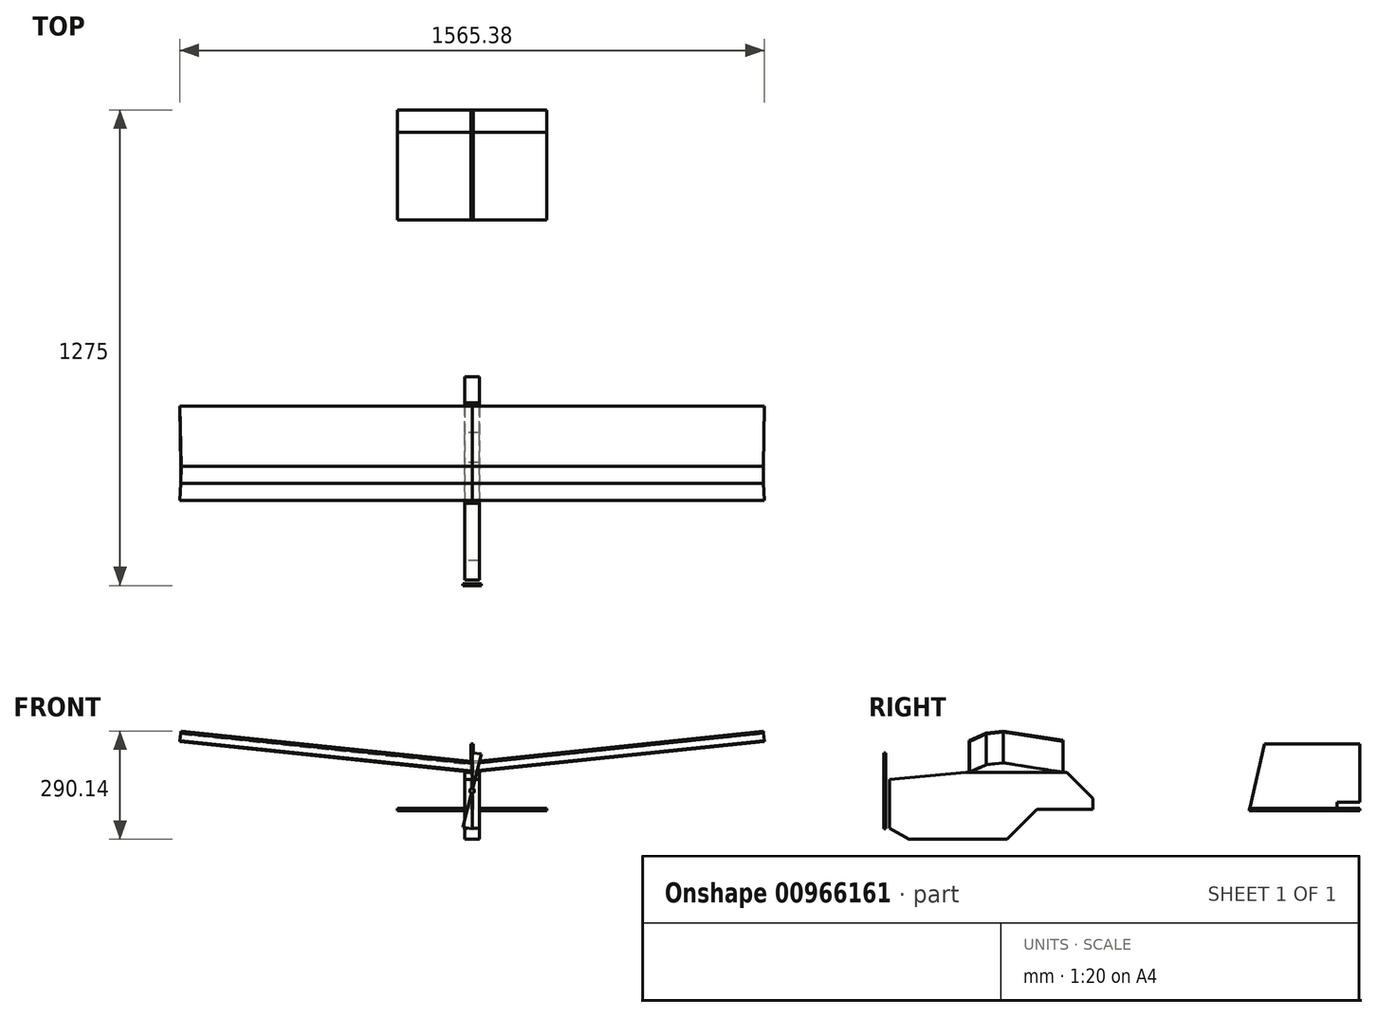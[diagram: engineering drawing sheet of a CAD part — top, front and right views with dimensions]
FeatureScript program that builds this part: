
annotation { "Feature Type Name" : "Feature", "Feature Type Description" : "" }
export const myFeature = defineFeature(function(context is Context, id is Id, definition is map)
    precondition{}
    {
        {
            var Q0;
            Q0=qCreatedBy(makeId("Right.planeOp"),FACE);
            var sketch = newSketch(context, id + "F0", { "sketchPlane" : qUnion([Q0])});
            skLineSegment(sketch, "E0", {"start": v(0, 0) * mm, "end": v(45, 20) * mm});
            skLineSegment(sketch, "E1", {"start": v(45, 20) * mm, "end": v(90, 25) * mm});
            skLineSegment(sketch, "E2", {"start": v(90, 25) * mm, "end": v(250, 0) * mm});
            skLineSegment(sketch, "E3.0", {"start": v(90.07, 28.03) * mm, "end": v(250.46, 2.96) * mm});
            skLineSegment(sketch, "E3.1", {"start": v(44.2, 22.93) * mm, "end": v(90.07, 28.03) * mm});
            skLineSegment(sketch, "E3.2", {"start": v(-1.22, 2.74) * mm, "end": v(44.2, 22.93) * mm});
            skLineSegment(sketch, "E4", {"start": v(0, 0) * mm, "end": v(-1.22, 2.74) * mm});
            skLineSegment(sketch, "E5", {"start": v(250, 0) * mm, "end": v(250.46, 2.96) * mm});
            skSolve(sketch);
        }
        {
            var Q0;
            Q0=makeQuery(id+"F0.imprint","IMPRINT",FACE,{"disambiguationData":[TD([[makeQuery(id+"F0.imprint","IMPRINT",EDGE,{"derivedFrom":sQuery(id+"F0.wireOp",EDGE,"E1")}),1.0]])]});
            var Q1;
            Q1=makeQuery(id+"F0.imprint","IMPRINT",FACE,{"disambiguationData":[TD([[makeQuery(id+"F0.imprint","IMPRINT",EDGE,{"derivedFrom":sQuery(id+"F0.wireOp",EDGE,"E0")}),1.0]])]});
            var Q2;
            Q2=makeQuery(id+"F0.imprint","IMPRINT",FACE,{"disambiguationData":[TD([[makeQuery(id+"F0.imprint","IMPRINT",EDGE,{"derivedFrom":sQuery(id+"F0.wireOp",EDGE,"E2")}),1.0]])]});
            extrude(context, id + "F1", {"entities" : qUnion([Q0, Q1, Q2]), "depth" : 787 * mm, "offsetDistance" : 25 * mm});
        }
        {
            var Q0;
            Q0=qCreatedBy(makeId("Front.planeOp"),FACE);
            var sketch = newSketch(context, id + "F2", { "sketchPlane" : qUnion([Q0])});
            skPoint(sketch, "E6.middle", {"position": v(0, 0) * mm});
            skLineSegment(sketch, "E7", {"start": v(0, 0) * mm, "end": v(32.96, -3.46) * mm, "construction": true});
            skLineSegment(sketch, "E8.bottom", {"start": v(0, 0) * mm, "end": v(-49.73, 5.23) * mm});
            skLineSegment(sketch, "E8.top", {"start": v(5.23, 49.73) * mm, "end": v(-44.5, 54.95) * mm});
            skLineSegment(sketch, "E8.left", {"start": v(0, 0) * mm, "end": v(5.23, 49.73) * mm});
            skLineSegment(sketch, "E8.right", {"start": v(-49.73, 5.23) * mm, "end": v(-44.5, 54.95) * mm});
            skSolve(sketch);
        }
        {
            var Q0;
            Q0=makeQuery(id+"F2.imprint","IMPRINT",FACE,{"disambiguationData":[TD([[makeQuery(id+"F2.imprint","IMPRINT",EDGE,{"derivedFrom":sQuery(id+"F2.wireOp",EDGE,"E8.bottom")}),-1.0]])]});
            extrude(context, id + "F3", {"entities" : qUnion([Q0]), "operationType" : NewBodyOperationType.REMOVE, "endBound" : BoundingType.THROUGH_ALL, "oppositeDirection" : true, "depth" : 300 * mm, "offsetDistance" : 25 * mm});
        }
        {
            var Q0;
            Q0=makeQuery(id+"F1.opExtrude","SWEPT_BODY",BODY,{"disambiguationData":[OSD([sQuery(id+"F0.wireOp",EDGE,"E0"),sQuery(id+"F0.wireOp",EDGE,"E1"),sQuery(id+"F0.wireOp",EDGE,"E2"),sQuery(id+"F0.wireOp",EDGE,"E3.0"),sQuery(id+"F0.wireOp",EDGE,"E3.1"),sQuery(id+"F0.wireOp",EDGE,"E3.2"),sQuery(id+"F0.wireOp",EDGE,"E4"),sQuery(id+"F0.wireOp",EDGE,"E5")])]});
            var Q1;
            Q1=qCreatedBy(makeId("Right.planeOp"),FACE);
            mirror(context, id + "F4", {"entities" : qUnion([Q0]), "mirrorPlane" : qUnion([Q1])});
        }
        {
            var Q0;
            Q0=qCreatedBy(makeId("Right.planeOp"),FACE);
            var sketch = newSketch(context, id + "F5", { "sketchPlane" : qUnion([Q0])});
            skLineSegment(sketch, "E9", {"start": v(-68.1, 0) * mm, "end": v(194.4, 0) * mm, "construction": true});
            skSolve(sketch);
        }
        {
            var Q0;
            Q0=makeQuery(id+"F4.opPattern","COPY",BODY,{"derivedFrom":makeQuery(id+"F1.opExtrude","SWEPT_BODY",BODY,{"disambiguationData":[OSD([sQuery(id+"F0.wireOp",EDGE,"E0"),sQuery(id+"F0.wireOp",EDGE,"E1"),sQuery(id+"F0.wireOp",EDGE,"E2"),sQuery(id+"F0.wireOp",EDGE,"E3.0"),sQuery(id+"F0.wireOp",EDGE,"E3.1"),sQuery(id+"F0.wireOp",EDGE,"E3.2"),sQuery(id+"F0.wireOp",EDGE,"E4"),sQuery(id+"F0.wireOp",EDGE,"E5")])]}),"instanceName":"1"});
            var Q1;
            Q1=sQuery(id+"F5.wireOp",EDGE,"E9");
            transform(context, id + "F6", {"entities" : qUnion([Q0]), "transformType" : TransformType.ROTATION, "transformAxis" : qUnion([Q1]), "angle" : 6 * degree, "makeCopy" : false});
        }
        {
            var Q0;
            Q0=makeQuery(id+"F1.opExtrude","SWEPT_BODY",BODY,{"disambiguationData":[OSD([sQuery(id+"F0.wireOp",EDGE,"E0"),sQuery(id+"F0.wireOp",EDGE,"E1"),sQuery(id+"F0.wireOp",EDGE,"E2"),sQuery(id+"F0.wireOp",EDGE,"E3.0"),sQuery(id+"F0.wireOp",EDGE,"E3.1"),sQuery(id+"F0.wireOp",EDGE,"E3.2"),sQuery(id+"F0.wireOp",EDGE,"E4"),sQuery(id+"F0.wireOp",EDGE,"E5")])]});
            var Q1;
            Q1=sQuery(id+"F5.wireOp",EDGE,"E9");
            transform(context, id + "F7", {"entities" : qUnion([Q0]), "transformType" : TransformType.ROTATION, "transformAxis" : qUnion([Q1]), "angle" : 6 * degree, "oppositeDirection" : true, "makeCopy" : false});
        }
        {
            var Q0;
            Q0=qCreatedBy(makeId("Top.planeOp"),FACE);
            var sketch = newSketch(context, id + "F8", { "sketchPlane" : qUnion([Q0])});
            skLineSegment(sketch, "E10.bottom", {"start": v(-200, 235) * mm, "end": v(200, 235) * mm});
            skLineSegment(sketch, "E10.top", {"start": v(-200, 0) * mm, "end": v(0, 0) * mm});
            skLineSegment(sketch, "E10.left", {"start": v(-200, 235) * mm, "end": v(-200, 0) * mm});
            skLineSegment(sketch, "E10.right", {"start": v(200, 235) * mm, "end": v(200, 0) * mm});
            skLineSegment(sketch, "E11", {"start": v(0, 0) * mm, "end": v(200, 0) * mm});
            skLineSegment(sketch, "E12.top", {"start": v(-200, 295) * mm, "end": v(200, 295) * mm});
            skLineSegment(sketch, "E12.left", {"start": v(-200, 235) * mm, "end": v(-200, 295) * mm});
            skLineSegment(sketch, "E12.right", {"start": v(200, 235) * mm, "end": v(200, 295) * mm});
            skSolve(sketch);
        }
        {
            var Q0;
            Q0=makeQuery(id+"F8.imprint","IMPRINT",FACE,{"disambiguationData":[TD([[makeQuery(id+"F8.imprint","IMPRINT",EDGE,{"derivedFrom":sQuery(id+"F8.wireOp",EDGE,"E10.top")}),1.0]])]});
            extrude(context, id + "F9", {"entities" : qUnion([Q0]), "endBound" : BoundingType.SYMMETRIC, "depth" : 6 * mm, "offsetDistance" : 25 * mm});
        }
        {
            var Q0;
            Q0=makeQuery(id+"F8.imprint","IMPRINT",FACE,{"disambiguationData":[TD([[makeQuery(id+"F8.imprint","IMPRINT",EDGE,{"derivedFrom":sQuery(id+"F8.wireOp",EDGE,"E10.bottom")}),1.0]])]});
            var Q1;
            Q1=sQuery(id+"F8.wireOp",EDGE,"E12.right");
            extrude(context, id + "F10", {"entities" : qUnion([Q0]), "surfaceEntities" : qUnion([Q1]), "endBound" : BoundingType.SYMMETRIC, "depth" : 6 * mm, "offsetDistance" : 25 * mm});
        }
        {
            var Q0;
            Q0=qCreatedBy(makeId("Right.planeOp"),FACE);
            var sketch = newSketch(context, id + "F11", { "sketchPlane" : qUnion([Q0])});
            skLineSegment(sketch, "E13", {"start": v(0, 0) * mm, "end": v(40, 175) * mm});
            skLineSegment(sketch, "E14", {"start": v(40, 175) * mm, "end": v(235, 175) * mm});
            skLineSegment(sketch, "E15", {"start": v(235, 175) * mm, "end": v(235, 0) * mm});
            skLineSegment(sketch, "E16", {"start": v(235, 0) * mm, "end": v(0, 0) * mm});
            skLineSegment(sketch, "E17.bottom", {"start": v(235, 175) * mm, "end": v(295, 175) * mm});
            skLineSegment(sketch, "E17.top", {"start": v(235, 20) * mm, "end": v(295, 20) * mm});
            skLineSegment(sketch, "E17.left", {"start": v(235, 175) * mm, "end": v(235, 20) * mm});
            skLineSegment(sketch, "E17.right", {"start": v(295, 175) * mm, "end": v(295, 20) * mm});
            skSolve(sketch);
        }
        {
            var Q0;
            {var subQ0=sQuery(id+"F11.wireOp",EDGE,"E17.bottom");Q0=qUnion([makeQuery(id+"F11.imprint","IMPRINT",FACE,{"disambiguationData":[TD([[makeQuery(id+"F11.imprint","IMPRINT",EDGE,{"derivedFrom":sQuery(id+"F11.wireOp",EDGE,"E13")}),-1.0]])]}),makeQuery(id+"F11.imprint","IMPRINT",FACE,{"disambiguationData":[TD([[makeQuery(id+"F11.imprint","IMPRINT",EDGE,{"derivedFrom":subQ0}),-1.0]])]})]);}
            extrude(context, id + "F12", {"entities" : qUnion([Q0]), "endBound" : BoundingType.SYMMETRIC, "oppositeDirection" : true, "depth" : 6 * mm, "offsetDistance" : 25 * mm});
        }
        {
            var Q0;
            Q0=makeQuery(id+"F9.opExtrude","SWEPT_BODY",BODY,{"disambiguationData":[OSD([sQuery(id+"F8.wireOp",EDGE,"E10.bottom"),sQuery(id+"F8.wireOp",EDGE,"E10.top"),sQuery(id+"F8.wireOp",EDGE,"E10.left"),sQuery(id+"F8.wireOp",EDGE,"E10.right"),sQuery(id+"F8.wireOp",EDGE,"E11")])]});
            var Q1;
            Q1=makeQuery(id+"F10.opExtrude","SWEPT_BODY",BODY,{"disambiguationData":[OSD([sQuery(id+"F8.wireOp",EDGE,"E10.bottom"),sQuery(id+"F8.wireOp",EDGE,"E12.top"),sQuery(id+"F8.wireOp",EDGE,"E12.left"),sQuery(id+"F8.wireOp",EDGE,"E12.right")])]});
            var Q2;
            Q2=makeQuery(id+"F12.opExtrude","SWEPT_BODY",BODY,{"disambiguationData":[OSD([sQuery(id+"F11.wireOp",EDGE,"E13"),sQuery(id+"F11.wireOp",EDGE,"E14"),sQuery(id+"F11.wireOp",EDGE,"E15"),sQuery(id+"F11.wireOp",EDGE,"E16"),sQuery(id+"F11.wireOp",EDGE,"E17.bottom"),sQuery(id+"F11.wireOp",EDGE,"E17.top"),sQuery(id+"F11.wireOp",EDGE,"E17.right")])]});
            transform(context, id + "F13", {"entities" : qUnion([Q0, Q1, Q2]), "transformType" : TransformType.TRANSLATION_3D, "dx" : 0 * mm, "dy" : 750 * mm, "dz" : -100 * mm, "makeCopy" : false});
        }
        {
            var Q0;
            Q0=qCreatedBy(makeId("Front.planeOp"),FACE);
            var sketch = newSketch(context, id + "F14", { "sketchPlane" : qUnion([Q0])});
            skCircle(sketch, "E18", {"center": v(0, 0) * mm, "radius": 6.35 * mm});
            skLineSegment(sketch, "E19", {"start": v(0, 6.35) * mm, "end": v(0, 101.6) * mm});
            skLineSegment(sketch, "E20", {"start": v(0, 101.6) * mm, "end": v(25.37, 98.38) * mm});
            skLineSegment(sketch, "E21", {"start": v(0, 0) * mm, "end": v(25.37, 98.38) * mm});
            skLineSegment(sketch, "E22", {"start": v(0, 0) * mm, "end": v(-25.37, -98.38) * mm});
            skLineSegment(sketch, "E23", {"start": v(-25.37, -98.38) * mm, "end": v(0, -101.6) * mm});
            skLineSegment(sketch, "E24", {"start": v(0, -101.6) * mm, "end": v(0, -6.35) * mm});
            skSolve(sketch);
        }
        {
            var Q0;
            Q0 = qSketchRegion(id + "F14", true);
            extrude(context, id + "F15", {"entities" : qUnion([Q0]), "depth" : 5 * mm, "offsetDistance" : 25 * mm});
        }
        {
            var Q0;
            Q0=makeQuery(id+"F15.opExtrude","SWEPT_BODY",BODY,{"disambiguationData":[OSD([sQuery(id+"F14.wireOp",EDGE,"E18"),sQuery(id+"F14.wireOp",EDGE,"E19"),sQuery(id+"F14.wireOp",EDGE,"E20"),sQuery(id+"F14.wireOp",EDGE,"E21"),sQuery(id+"F14.wireOp",EDGE,"E22"),sQuery(id+"F14.wireOp",EDGE,"E23"),sQuery(id+"F14.wireOp",EDGE,"E24")])]});
            transform(context, id + "F16", {"entities" : qUnion([Q0]), "transformType" : TransformType.TRANSLATION_3D, "dx" : 0 * mm, "dy" : -225 * mm, "dz" : -50 * mm, "makeCopy" : false});
        }
        {
            var Q0;
            Q0=qCreatedBy(makeId("Right.planeOp"),FACE);
            var sketch = newSketch(context, id + "F17", { "sketchPlane" : qUnion([Q0])});
            skLineSegment(sketch, "E25", {"start": v(0, 0) * mm, "end": v(-10, 0) * mm});
            skLineSegment(sketch, "E26", {"start": v(-10, 0) * mm, "end": v(-215, -20) * mm});
            skLineSegment(sketch, "E27", {"start": v(-215, -20) * mm, "end": v(-215, -150) * mm});
            skLineSegment(sketch, "E28", {"start": v(-215, -150) * mm, "end": v(-163.04, -180) * mm});
            skLineSegment(sketch, "E29", {"start": v(-163.04, -180) * mm, "end": v(100, -180) * mm});
            skLineSegment(sketch, "E30", {"start": v(100, -180) * mm, "end": v(180, -100) * mm});
            skLineSegment(sketch, "E31", {"start": v(180, -100) * mm, "end": v(330, -100) * mm});
            skLineSegment(sketch, "E32", {"start": v(330, -100) * mm, "end": v(330, -70) * mm});
            skLineSegment(sketch, "E33", {"start": v(330, -70) * mm, "end": v(260, 0) * mm});
            skLineSegment(sketch, "E34", {"start": v(260, 0) * mm, "end": v(-10, 0) * mm});
            skSolve(sketch);
        }
        {
            var Q0;
            {var subQ0=sQuery(id+"F17.wireOp",EDGE,"E26");Q0=makeQuery(id+"F17.imprint","IMPRINT",FACE,{"disambiguationData":[TD([[makeQuery(id+"F17.imprint","IMPRINT",EDGE,{"derivedFrom":subQ0}),1.0]])]});}
            extrude(context, id + "F18", {"entities" : qUnion([Q0]), "endBound" : BoundingType.SYMMETRIC, "depth" : 40 * mm, "offsetDistance" : 25 * mm});
        }
    });
